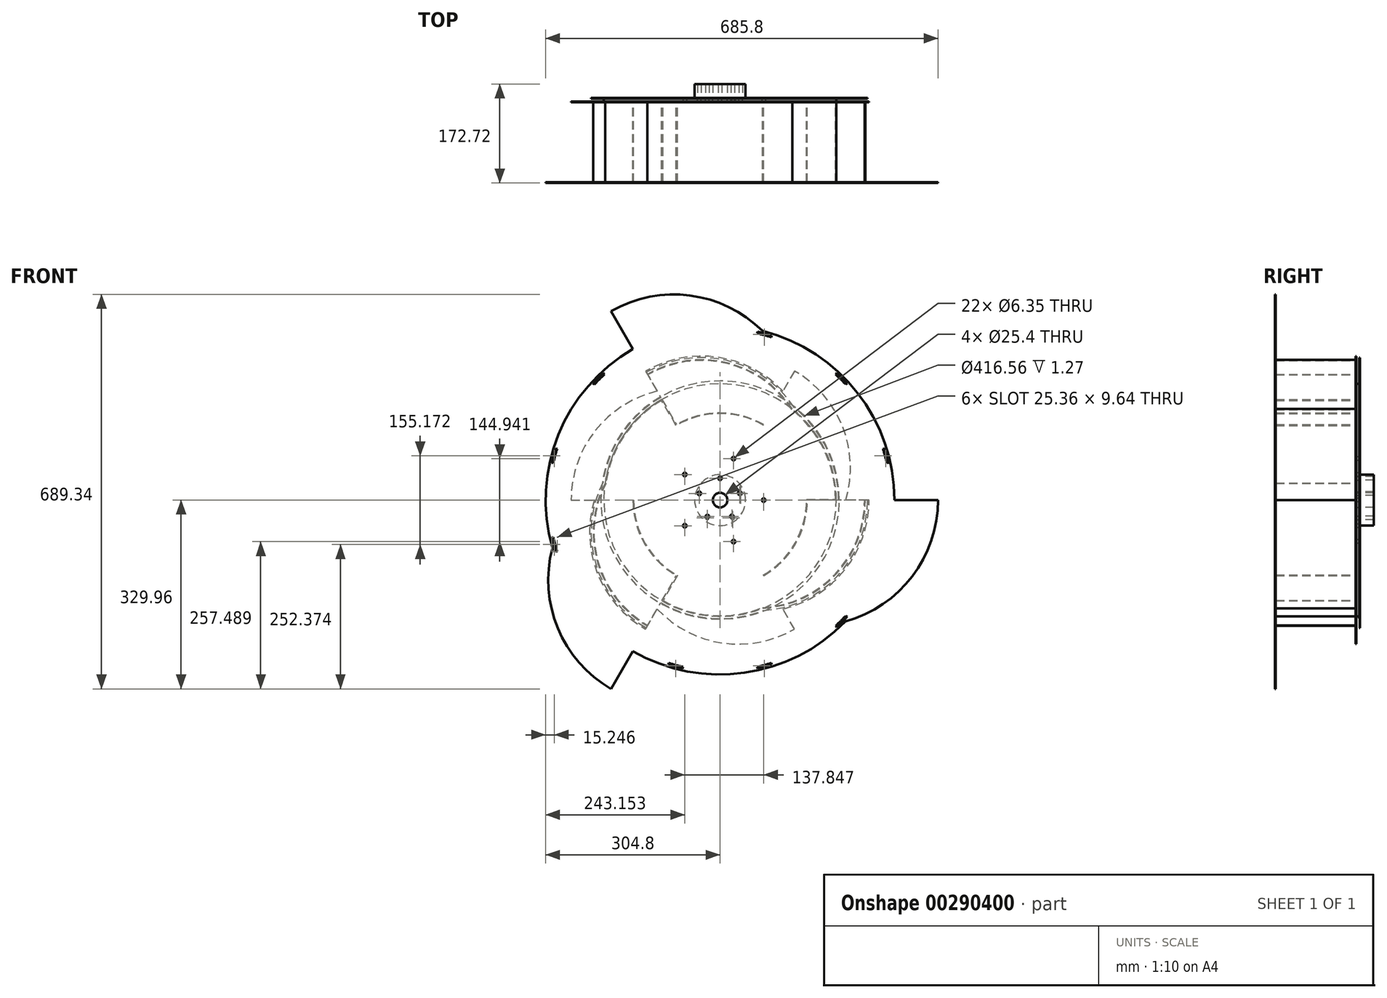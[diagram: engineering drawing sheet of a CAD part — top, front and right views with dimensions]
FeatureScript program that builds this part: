
annotation { "Feature Type Name" : "Feature", "Feature Type Description" : "" }
export const myFeature = defineFeature(function(context is Context, id is Id, definition is map)
    precondition{}
    {
        {
            var Q0;
            Q0=qCreatedBy(makeId("Front.planeOp"),FACE);
            var sketch = newSketch(context, id + "F0", { "sketchPlane" : qUnion([Q0])});
            skCircle(sketch, "E0", {"center": v(0, 0) * mm, "radius": 203.2 * mm});
            skCircle(sketch, "E1", {"center": v(0, 0) * mm, "radius": 12.7 * mm});
            skCircle(sketch, "E2", {"center": v(0, 38.1) * mm, "radius": 3.18 * mm});
            skCircle(sketch, "E3.1.0", {"center": v(-36.24, 11.77) * mm, "radius": 3.18 * mm});
            skCircle(sketch, "E3.2.0", {"center": v(-22.4, -30.82) * mm, "radius": 3.18 * mm});
            skCircle(sketch, "E3.3.0", {"center": v(22.4, -30.82) * mm, "radius": 3.18 * mm});
            skCircle(sketch, "E3.4.0", {"center": v(36.24, 11.77) * mm, "radius": 3.18 * mm});
            skLineSegment(sketch, "E4", {"start": v(0, 38.1) * mm, "end": v(36.24, 11.77) * mm, "construction": true});
            skLineSegment(sketch, "E5", {"start": v(36.24, 11.77) * mm, "end": v(22.4, -30.82) * mm, "construction": true});
            skLineSegment(sketch, "E6", {"start": v(22.4, -30.82) * mm, "end": v(-22.4, -30.82) * mm, "construction": true});
            skLineSegment(sketch, "E7", {"start": v(-22.4, -30.82) * mm, "end": v(-36.24, 11.77) * mm, "construction": true});
            skLineSegment(sketch, "E8", {"start": v(-36.24, 11.77) * mm, "end": v(0, 38.1) * mm, "construction": true});
            skSolve(sketch);
        }
        {
            var Q0;
            Q0=makeQuery(id+"F0.imprint","IMPRINT",FACE,{"disambiguationData":[TD([[makeQuery(id+"F0.imprint","IMPRINT",EDGE,{"derivedFrom":sQuery(id+"F0.wireOp",EDGE,"E0")}),1.0]])]});
            extrude(context, id + "F1", {"entities" : qUnion([Q0]), "depth" : 6.35 * mm});
        }
        {
            var Q0;
            Q0=makeQuery(id+"F1.opExtrude","CAP_FACE",FACE,{"disambiguationData":[OSD([sQuery(id+"F0.wireOp",EDGE,"E0"),sQuery(id+"F0.wireOp",EDGE,"E1"),sQuery(id+"F0.wireOp",EDGE,"E2"),sQuery(id+"F0.wireOp",EDGE,"E3.1.0"),sQuery(id+"F0.wireOp",EDGE,"E3.2.0"),sQuery(id+"F0.wireOp",EDGE,"E3.3.0"),sQuery(id+"F0.wireOp",EDGE,"E3.4.0")])],"isStart":true});
            var sketch = newSketch(context, id + "F2", { "sketchPlane" : qUnion([Q0])});
            skCircle(sketch, "E9", {"center": v(0, 0) * mm, "radius": 44.45 * mm});
            skCircle(sketch, "E10", {"center": v(0, 0) * mm, "radius": 12.7 * mm});
            skCircle(sketch, "E11", {"center": v(0, 38.1) * mm, "radius": 3.18 * mm});
            skCircle(sketch, "E12", {"center": v(36.24, 11.77) * mm, "radius": 3.18 * mm});
            skCircle(sketch, "E13", {"center": v(22.4, -30.82) * mm, "radius": 3.18 * mm});
            skCircle(sketch, "E14", {"center": v(-22.4, -30.82) * mm, "radius": 3.18 * mm});
            skCircle(sketch, "E15", {"center": v(-36.24, 11.77) * mm, "radius": 3.18 * mm});
            skSolve(sketch);
        }
        {
            var Q0;
            Q0=qSketchRegion(id+"F2",true);
            extrude(context, id + "F3", {"entities" : qUnion([Q0]), "depth" : 25.4 * mm});
        }
        {
            var Q0;
            Q0=makeQuery(id+"F3.opExtrude","CAP_FACE",FACE,{"disambiguationData":[OSD([sQuery(id+"F2.wireOp",EDGE,"E9"),sQuery(id+"F2.wireOp",EDGE,"E10"),sQuery(id+"F2.wireOp",EDGE,"E11"),sQuery(id+"F2.wireOp",EDGE,"E12"),sQuery(id+"F2.wireOp",EDGE,"E13"),sQuery(id+"F2.wireOp",EDGE,"E14"),sQuery(id+"F2.wireOp",EDGE,"E15")])],"isStart":false});
            cPlane(context, id + "F4", {"entities" : qUnion([Q0]), "cplaneType" : CPlaneType.OFFSET, "offset" : 25.4 * mm, "width" : 152.4 * mm, "height" : 152.4 * mm});
        }
        {
            var Q0;
            Q0=qCreatedBy(id+"F4.planeOp",FACE);
            var sketch = newSketch(context, id + "F5", { "sketchPlane" : qUnion([Q0])});
            skArc(sketch, "E16", {"start": v(-12.3, -3.17) * mm, "mid": v(12.7, 0) * mm, "end": v(-12.3, 3.17) * mm});
            skLineSegment(sketch, "E17", {"start": v(0, 0) * mm, "end": v(-12.7, 0) * mm, "construction": true});
            skLineSegment(sketch, "E18.bottom", {"start": v(-12.3, -3.18) * mm, "end": v(-9.76, -3.18) * mm});
            skLineSegment(sketch, "E18.top", {"start": v(-12.3, 3.17) * mm, "end": v(-9.76, 3.18) * mm});
            skLineSegment(sketch, "E18.right", {"start": v(-9.76, -3.17) * mm, "end": v(-9.76, 3.17) * mm});
            skLineSegment(sketch, "E19", {"start": v(-12.3, -3.17) * mm, "end": v(-12.3, 3.17) * mm, "construction": true});
            skSolve(sketch);
        }
        {
            var Q0;
            Q0=qSketchRegion(id+"F5",true);
            extrude(context, id + "F6", {"entities" : qUnion([Q0]), "oppositeDirection" : true, "depth" : 304.8 * mm});
        }
        {
            var Q0;
            Q0=makeQuery(id+"F1.opExtrude","CAP_FACE",FACE,{"disambiguationData":[OSD([sQuery(id+"F0.wireOp",EDGE,"E0"),sQuery(id+"F0.wireOp",EDGE,"E1"),sQuery(id+"F0.wireOp",EDGE,"E2"),sQuery(id+"F0.wireOp",EDGE,"E3.1.0"),sQuery(id+"F0.wireOp",EDGE,"E3.2.0"),sQuery(id+"F0.wireOp",EDGE,"E3.3.0"),sQuery(id+"F0.wireOp",EDGE,"E3.4.0")])],"isStart":false});
            var sketch = newSketch(context, id + "F7", { "sketchPlane" : qUnion([Q0])});
            skLineSegment(sketch, "E20", {"start": v(0, 0) * mm, "end": v(0, 203.2) * mm, "construction": true});
            skLineSegment(sketch, "E21", {"start": v(0, 203.2) * mm, "end": v(203.2, 0) * mm, "construction": true});
            skLineSegment(sketch, "E22", {"start": v(203.2, 0) * mm, "end": v(0, -203.2) * mm, "construction": true});
            skLineSegment(sketch, "E23", {"start": v(0, -203.2) * mm, "end": v(-203.2, 0) * mm, "construction": true});
            skLineSegment(sketch, "E24", {"start": v(-203.2, 0) * mm, "end": v(0, 203.2) * mm, "construction": true});
            skArc(sketch, "E25", {"start": v(0, 203.2) * mm, "mid": v(-143.68, 143.68) * mm, "end": v(-203.2, 0) * mm});
            skArc(sketch, "E26", {"start": v(0, 196.85) * mm, "mid": v(-139.2, 139.2) * mm, "end": v(-196.85, 0) * mm});
            skLineSegment(sketch, "E27", {"start": v(-203.2, 0) * mm, "end": v(-196.85, 0) * mm});
            skLineSegment(sketch, "E28", {"start": v(0, 203.2) * mm, "end": v(0, 196.85) * mm});
            skArc(sketch, "E29", {"start": v(279.4, 0) * mm, "mid": v(172.74, 147.03) * mm, "end": v(0, 203.2) * mm});
            skLineSegment(sketch, "E30", {"start": v(203.2, 0) * mm, "end": v(203.2, -92.56) * mm, "construction": true});
            skLineSegment(sketch, "E31", {"start": v(203.2, 0) * mm, "end": v(279.4, 0) * mm, "construction": true});
            skLineSegment(sketch, "E32", {"start": v(0, 203.2) * mm, "end": v(0, 209.55) * mm, "construction": true});
            skArc(sketch, "E33", {"start": v(0, 203.2) * mm, "mid": v(-38.81, 199.46) * mm, "end": v(-76.2, 188.37) * mm});
            skLineSegment(sketch, "E34", {"start": v(279.4, 0) * mm, "end": v(285.75, 0) * mm, "construction": true});
            skArc(sketch, "E35", {"start": v(285.75, 0) * mm, "mid": v(177.18, 151.55) * mm, "end": v(0, 209.55) * mm});
            skLineSegment(sketch, "E36", {"start": v(279.4, 0) * mm, "end": v(285.75, 0) * mm});
            skLineSegment(sketch, "E37", {"start": v(-76.2, 188.37) * mm, "end": v(-100.1, 178.7) * mm, "construction": true});
            skLineSegment(sketch, "E38", {"start": v(-76.2, 188.37) * mm, "end": v(-78.58, 194.26) * mm});
            skArc(sketch, "E39", {"start": v(0, 209.55) * mm, "mid": v(-40.03, 205.7) * mm, "end": v(-78.58, 194.26) * mm});
            skSolve(sketch);
        }
        {
            var Q0;
            Q0=qSketchRegion(id+"F7",true);
            extrude(context, id + "F8", {"entities" : qUnion([Q0]), "depth" : 152.4 * mm});
        }
        {
            var Q0;
            Q0=makeQuery(id+"F8.opExtrude","SWEPT_BODY",BODY,{"disambiguationData":[OSD([sQuery(id+"F7.wireOp",EDGE,"E25"),sQuery(id+"F7.wireOp",EDGE,"E26"),sQuery(id+"F7.wireOp",EDGE,"E27"),sQuery(id+"F7.wireOp",EDGE,"E28"),sQuery(id+"F7.wireOp",EDGE,"E29"),sQuery(id+"F7.wireOp",EDGE,"E35"),sQuery(id+"F7.wireOp",EDGE,"E36"),sQuery(id+"F7.wireOp",EDGE,"E38"),sQuery(id+"F7.wireOp",EDGE,"E39")])]});
            deleteBodies(context, id + "F9", {"entities" : qUnion([Q0])});
        }
        {
            var Q0;
            Q0=makeQuery(id+"F1.opExtrude","CAP_FACE",FACE,{"disambiguationData":[OSD([sQuery(id+"F0.wireOp",EDGE,"E0"),sQuery(id+"F0.wireOp",EDGE,"E1"),sQuery(id+"F0.wireOp",EDGE,"E2"),sQuery(id+"F0.wireOp",EDGE,"E3.1.0"),sQuery(id+"F0.wireOp",EDGE,"E3.2.0"),sQuery(id+"F0.wireOp",EDGE,"E3.3.0"),sQuery(id+"F0.wireOp",EDGE,"E3.4.0")])],"isStart":false});
            var sketch = newSketch(context, id + "F10", { "sketchPlane" : qUnion([Q0])});
            skLineSegment(sketch, "E40", {"start": v(0, 0) * mm, "end": v(203.2, 0) * mm, "construction": true});
            skLineSegment(sketch, "E41", {"start": v(203.2, 0) * mm, "end": v(203.2, 0) * mm});
            skLineSegment(sketch, "E42", {"start": v(203.2, 0) * mm, "end": v(524, 0) * mm, "construction": true});
            skArc(sketch, "E43", {"start": v(74.61, -189) * mm, "mid": v(202.01, -130.3) * mm, "end": v(254, 0) * mm});
            skLineSegment(sketch, "E44", {"start": v(0, 0) * mm, "end": v(-101.6, -175.98) * mm, "construction": true});
            skLineSegment(sketch, "E45", {"start": v(0, 0) * mm, "end": v(-101.6, 175.98) * mm, "construction": true});
            skLineSegment(sketch, "E46", {"start": v(-101.6, -175.98) * mm, "end": v(-76.2, -131.98) * mm});
            skArc(sketch, "E47", {"start": v(-152.4, 0) * mm, "mid": v(-131.98, -76.2) * mm, "end": v(-76.2, -131.98) * mm});
            skCircle(sketch, "E48", {"center": v(0, 0) * mm, "radius": 152.4 * mm, "construction": true});
            skLineSegment(sketch, "E49", {"start": v(-152.4, 0) * mm, "end": v(-151.13, 0) * mm});
            skArc(sketch, "E50", {"start": v(-151.13, 0) * mm, "mid": v(-130.56, -76.11) * mm, "end": v(-74.46, -131.51) * mm});
            skLineSegment(sketch, "E51", {"start": v(-74.46, -131.51) * mm, "end": v(-99.86, -175.5) * mm});
            skArc(sketch, "E52", {"start": v(74.34, -187.75) * mm, "mid": v(201.02, -129.5) * mm, "end": v(252.73, 0) * mm});
            skLineSegment(sketch, "E53", {"start": v(252.73, 0) * mm, "end": v(254, 0) * mm});
            skArc(sketch, "E54.trimOffspring", {"start": v(-101.6, 175.98) * mm, "mid": v(-182.99, -88.35) * mm, "end": v(74.61, -189) * mm, "construction": true});
            skArc(sketch, "E55", {"start": v(-99.86, -175.5) * mm, "mid": v(-14.15, -201.43) * mm, "end": v(74.34, -187.75) * mm});
            skArc(sketch, "E56", {"start": v(-101.6, -175.98) * mm, "mid": v(-14.98, -202.65) * mm, "end": v(74.61, -189) * mm});
            skArc(sketch, "E57.1.0", {"start": v(76.2, -131.98) * mm, "mid": v(131.98, -76.2) * mm, "end": v(152.4, 0) * mm});
            skArc(sketch, "E57.1.1", {"start": v(75.56, -130.88) * mm, "mid": v(131.2, -75.01) * mm, "end": v(151.12, 1.27) * mm});
            skLineSegment(sketch, "E57.1.2", {"start": v(151.12, 1.27) * mm, "end": v(201.93, 1.27) * mm});
            skArc(sketch, "E57.1.3", {"start": v(201.93, 1.27) * mm, "mid": v(181.52, 88.46) * mm, "end": v(125.43, 158.25) * mm});
            skLineSegment(sketch, "E57.1.4", {"start": v(203.2, 0) * mm, "end": v(152.4, 0) * mm});
            skArc(sketch, "E57.1.5", {"start": v(203.2, 0) * mm, "mid": v(182.99, 88.35) * mm, "end": v(126.38, 159.12) * mm});
            skArc(sketch, "E57.1.6", {"start": v(126.38, 159.12) * mm, "mid": v(11.83, 240.1) * mm, "end": v(-127, 219.97) * mm});
            skArc(sketch, "E57.1.7", {"start": v(125.43, 158.25) * mm, "mid": v(11.63, 238.84) * mm, "end": v(-126.36, 218.87) * mm});
            skLineSegment(sketch, "E57.1.8", {"start": v(-126.36, 218.87) * mm, "end": v(-127, 219.97) * mm});
            skArc(sketch, "E57.2.0", {"start": v(76.2, 131.98) * mm, "mid": v(0, 152.4) * mm, "end": v(-76.2, 131.98) * mm});
            skArc(sketch, "E57.2.1", {"start": v(75.57, 130.88) * mm, "mid": v(-0.64, 151.13) * mm, "end": v(-76.66, 130.24) * mm});
            skLineSegment(sketch, "E57.2.2", {"start": v(-76.66, 130.24) * mm, "end": v(-102.06, 174.24) * mm});
            skArc(sketch, "E57.2.3", {"start": v(-102.06, 174.24) * mm, "mid": v(-167.37, 112.97) * mm, "end": v(-199.76, 29.5) * mm});
            skLineSegment(sketch, "E57.2.4", {"start": v(-101.6, 175.98) * mm, "end": v(-76.2, 131.98) * mm});
            skArc(sketch, "E57.2.5", {"start": v(-101.6, 175.98) * mm, "mid": v(-168, 114.3) * mm, "end": v(-201, 29.89) * mm});
            skArc(sketch, "E57.2.6", {"start": v(-201, 29.89) * mm, "mid": v(-213.84, -109.8) * mm, "end": v(-127, -219.97) * mm});
            skArc(sketch, "E57.2.7", {"start": v(-199.76, 29.5) * mm, "mid": v(-212.65, -109.34) * mm, "end": v(-126.37, -218.87) * mm});
            skLineSegment(sketch, "E57.2.8", {"start": v(-126.37, -218.87) * mm, "end": v(-127, -219.97) * mm});
            skLineSegment(sketch, "E58", {"start": v(75.56, -130.88) * mm, "end": v(76.2, -131.98) * mm});
            skLineSegment(sketch, "E59", {"start": v(75.57, 130.88) * mm, "end": v(76.2, 131.98) * mm});
            skSolve(sketch);
        }
        {
            var Q0;
            Q0=qSketchRegion(id+"F10",true);
            extrude(context, id + "F11", {"entities" : qUnion([Q0]), "depth" : 139.7 * mm});
        }
        {
            var Q0;
            Q0=makeQuery(id+"F11.opExtrude","CAP_FACE",FACE,{"disambiguationData":[OSD([sQuery(id+"F10.wireOp",EDGE,"E57.2.0"),sQuery(id+"F10.wireOp",EDGE,"E57.2.1"),sQuery(id+"F10.wireOp",EDGE,"E57.2.2"),sQuery(id+"F10.wireOp",EDGE,"E57.2.3"),sQuery(id+"F10.wireOp",EDGE,"E57.2.4"),sQuery(id+"F10.wireOp",EDGE,"E57.2.5"),sQuery(id+"F10.wireOp",EDGE,"E57.2.6"),sQuery(id+"F10.wireOp",EDGE,"E57.2.7"),sQuery(id+"F10.wireOp",EDGE,"E57.2.8"),sQuery(id+"F10.wireOp",EDGE,"E59")])],"isStart":false});
            var sketch = newSketch(context, id + "F12", { "sketchPlane" : qUnion([Q0])});
            skArc(sketch, "E60", {"start": v(-152.4, -263.96) * mm, "mid": v(42.3, -301.85) * mm, "end": v(219.07, -211.92) * mm});
            skArc(sketch, "E61", {"start": v(-293.06, -83.77) * mm, "mid": v(-283.43, -224.21) * mm, "end": v(-190.5, -329.96) * mm});
            skLineSegment(sketch, "E62", {"start": v(-190.5, -329.96) * mm, "end": v(-152.4, -263.96) * mm});
            skLineSegment(sketch, "E63", {"start": v(-152.4, -263.96) * mm, "end": v(-59.03, -317.87) * mm, "construction": true});
            skArc(sketch, "E64.1.0", {"start": v(219.07, -211.92) * mm, "mid": v(335.89, -133.35) * mm, "end": v(381, 0) * mm});
            skLineSegment(sketch, "E64.1.1", {"start": v(381, 0) * mm, "end": v(304.8, 0) * mm});
            skArc(sketch, "E64.2.0", {"start": v(73.99, 295.68) * mm, "mid": v(-52.46, 357.56) * mm, "end": v(-190.5, 329.96) * mm});
            skLineSegment(sketch, "E64.2.1", {"start": v(-190.5, 329.96) * mm, "end": v(-152.4, 263.96) * mm});
            skArc(sketch, "E65.trimOffspring", {"start": v(304.8, 0) * mm, "mid": v(240.27, 187.55) * mm, "end": v(73.99, 295.68) * mm});
            skArc(sketch, "E66.trimOffspring", {"start": v(-152.4, 263.96) * mm, "mid": v(-282.56, 114.3) * mm, "end": v(-293.06, -83.77) * mm});
            skSolve(sketch);
        }
        {
            var Q0;
            Q0=qSketchRegion(id+"F12",true);
            extrude(context, id + "F13", {"entities" : qUnion([Q0]), "depth" : 1.27 * mm});
        }
        {
            var Q0;
            Q0=makeQuery(id+"F13.opExtrude","CAP_FACE",FACE,{"disambiguationData":[OSD([sQuery(id+"F12.wireOp",EDGE,"E60"),sQuery(id+"F12.wireOp",EDGE,"E61"),sQuery(id+"F12.wireOp",EDGE,"E62"),sQuery(id+"F12.wireOp",EDGE,"E64.1.0"),sQuery(id+"F12.wireOp",EDGE,"E64.1.1"),sQuery(id+"F12.wireOp",EDGE,"E64.2.0"),sQuery(id+"F12.wireOp",EDGE,"E64.2.1"),sQuery(id+"F12.wireOp",EDGE,"E65.trimOffspring"),sQuery(id+"F12.wireOp",EDGE,"E66.trimOffspring")])],"isStart":false});
            var sketch = newSketch(context, id + "F14", { "sketchPlane" : qUnion([Q0])});
            skCircle(sketch, "E67", {"center": v(0, 0) * mm, "radius": 76.2 * mm, "construction": true});
            skCircle(sketch, "E68", {"center": v(76.2, 0) * mm, "radius": 3.18 * mm});
            skCircle(sketch, "E69.1.0", {"center": v(23.55, 72.47) * mm, "radius": 3.18 * mm});
            skCircle(sketch, "E69.2.0", {"center": v(-61.65, 44.79) * mm, "radius": 3.18 * mm});
            skCircle(sketch, "E69.3.0", {"center": v(-61.65, -44.79) * mm, "radius": 3.18 * mm});
            skCircle(sketch, "E69.4.0", {"center": v(23.55, -72.47) * mm, "radius": 3.18 * mm});
            skLineSegment(sketch, "E70", {"start": v(0, 0) * mm, "end": v(0, 176.8) * mm, "construction": true});
            skCircle(sketch, "E71", {"center": v(0, 0) * mm, "radius": 12.7 * mm});
            skSolve(sketch);
        }
        {
            var Q0;
            Q0=qSketchRegion(id+"F14",true);
            extrude(context, id + "F15", {"entities" : qUnion([Q0]), "operationType" : NewBodyOperationType.REMOVE, "endBound" : BoundingType.THROUGH_ALL, "oppositeDirection" : true, "depth" : 25.4 * mm});
        }
        {
            var Q0;
            Q0=makeQuery(id+"F13.opExtrude","CAP_FACE",FACE,{"disambiguationData":[OSD([sQuery(id+"F12.wireOp",EDGE,"E60"),sQuery(id+"F12.wireOp",EDGE,"E61"),sQuery(id+"F12.wireOp",EDGE,"E62"),sQuery(id+"F12.wireOp",EDGE,"E64.1.0"),sQuery(id+"F12.wireOp",EDGE,"E64.1.1"),sQuery(id+"F12.wireOp",EDGE,"E64.2.0"),sQuery(id+"F12.wireOp",EDGE,"E64.2.1"),sQuery(id+"F12.wireOp",EDGE,"E65.trimOffspring"),sQuery(id+"F12.wireOp",EDGE,"E66.trimOffspring")])],"isStart":true});
            var sketch = newSketch(context, id + "F16", { "sketchPlane" : qUnion([Q0])});
            skCircle(sketch, "E72", {"center": v(-23.55, -72.47) * mm, "radius": 6.35 * mm});
            skCircle(sketch, "E73", {"center": v(0, 0) * mm, "radius": 76.2 * mm, "construction": true});
            skCircle(sketch, "E74.1.0", {"center": v(61.65, -44.79) * mm, "radius": 6.35 * mm});
            skCircle(sketch, "E74.2.0", {"center": v(61.65, 44.79) * mm, "radius": 6.35 * mm});
            skCircle(sketch, "E74.3.0", {"center": v(-23.55, 72.47) * mm, "radius": 6.35 * mm});
            skCircle(sketch, "E74.4.0", {"center": v(-76.2, 0) * mm, "radius": 6.35 * mm});
            skSolve(sketch);
        }
        {
            var Q0;
            Q0=makeQuery(id+"F13.opExtrude","CAP_FACE",FACE,{"disambiguationData":[OSD([sQuery(id+"F12.wireOp",EDGE,"E60"),sQuery(id+"F12.wireOp",EDGE,"E61"),sQuery(id+"F12.wireOp",EDGE,"E62"),sQuery(id+"F12.wireOp",EDGE,"E64.1.0"),sQuery(id+"F12.wireOp",EDGE,"E64.1.1"),sQuery(id+"F12.wireOp",EDGE,"E64.2.0"),sQuery(id+"F12.wireOp",EDGE,"E64.2.1"),sQuery(id+"F12.wireOp",EDGE,"E65.trimOffspring"),sQuery(id+"F12.wireOp",EDGE,"E66.trimOffspring")])],"isStart":false});
            var sketch = newSketch(context, id + "F17", { "sketchPlane" : qUnion([Q0])});
            skCircle(sketch, "E75", {"center": v(0, 0) * mm, "radius": 304.8 * mm, "construction": true});
            skLineSegment(sketch, "E76", {"start": v(0, 0) * mm, "end": v(0, 304.8) * mm, "construction": true});
            skLineSegment(sketch, "E77", {"start": v(73.99, 295.68) * mm, "end": v(213.6, 260.75) * mm, "construction": true});
            skLineSegment(sketch, "E78", {"start": v(0, 0) * mm, "end": v(215.53, 215.53) * mm, "construction": true});
            skArc(sketch, "E79", {"start": v(222.07, 204.11) * mm, "mid": v(213.28, 213.28) * mm, "end": v(204.11, 222.07) * mm});
            skPoint(sketch, "E80", {"position": v(213.28, 213.28) * mm});
            skArc(sketch, "E81", {"start": v(219.83, 201.86) * mm, "mid": v(211.04, 211.04) * mm, "end": v(201.86, 219.83) * mm});
            skPoint(sketch, "E82", {"position": v(211.04, 211.04) * mm});
            skLineSegment(sketch, "E83", {"start": v(204.11, 222.07) * mm, "end": v(201.86, 219.83) * mm});
            skLineSegment(sketch, "E84", {"start": v(222.07, 204.11) * mm, "end": v(219.83, 201.86) * mm});
            skLineSegment(sketch, "E85", {"start": v(211.04, 211.04) * mm, "end": v(233.3, 188.78) * mm, "construction": true});
            skArc(sketch, "E86.1.0", {"start": v(294.38, 65.73) * mm, "mid": v(291.35, 78.07) * mm, "end": v(287.8, 90.26) * mm});
            skPoint(sketch, "E86.1.1", {"position": v(288.28, 77.24) * mm});
            skPoint(sketch, "E86.1.2", {"position": v(291.35, 78.07) * mm});
            skArc(sketch, "E86.1.3", {"start": v(291.3, 64.9) * mm, "mid": v(288.28, 77.24) * mm, "end": v(284.73, 89.44) * mm});
            skLineSegment(sketch, "E86.1.4", {"start": v(294.38, 65.73) * mm, "end": v(291.3, 64.9) * mm});
            skLineSegment(sketch, "E86.1.5", {"start": v(287.8, 90.26) * mm, "end": v(284.73, 89.44) * mm});
            skArc(sketch, "E86.2.0", {"start": v(287.8, -90.26) * mm, "mid": v(291.35, -78.07) * mm, "end": v(294.38, -65.73) * mm, "construction": true});
            skPoint(sketch, "E86.2.1", {"position": v(288.28, -77.24) * mm});
            skPoint(sketch, "E86.2.2", {"position": v(291.35, -78.07) * mm});
            skArc(sketch, "E86.2.3", {"start": v(284.73, -89.44) * mm, "mid": v(288.28, -77.24) * mm, "end": v(291.3, -64.9) * mm, "construction": true});
            skLineSegment(sketch, "E86.2.4", {"start": v(287.8, -90.26) * mm, "end": v(284.73, -89.44) * mm, "construction": true});
            skLineSegment(sketch, "E86.2.5", {"start": v(294.38, -65.73) * mm, "end": v(291.3, -64.9) * mm, "construction": true});
            skArc(sketch, "E86.3.0", {"start": v(204.11, -222.07) * mm, "mid": v(213.28, -213.28) * mm, "end": v(222.07, -204.11) * mm});
            skPoint(sketch, "E86.3.1", {"position": v(211.04, -211.04) * mm});
            skPoint(sketch, "E86.3.2", {"position": v(213.28, -213.28) * mm});
            skArc(sketch, "E86.3.3", {"start": v(201.86, -219.83) * mm, "mid": v(211.04, -211.04) * mm, "end": v(219.83, -201.86) * mm});
            skLineSegment(sketch, "E86.3.4", {"start": v(204.11, -222.07) * mm, "end": v(201.86, -219.83) * mm});
            skLineSegment(sketch, "E86.3.5", {"start": v(222.07, -204.11) * mm, "end": v(219.83, -201.86) * mm});
            skArc(sketch, "E86.4.0", {"start": v(65.73, -294.38) * mm, "mid": v(78.07, -291.35) * mm, "end": v(90.26, -287.8) * mm});
            skPoint(sketch, "E86.4.1", {"position": v(77.24, -288.28) * mm});
            skPoint(sketch, "E86.4.2", {"position": v(78.07, -291.35) * mm});
            skArc(sketch, "E86.4.3", {"start": v(64.9, -291.3) * mm, "mid": v(77.24, -288.28) * mm, "end": v(89.44, -284.73) * mm});
            skLineSegment(sketch, "E86.4.4", {"start": v(65.73, -294.38) * mm, "end": v(64.9, -291.3) * mm});
            skLineSegment(sketch, "E86.4.5", {"start": v(90.26, -287.8) * mm, "end": v(89.44, -284.73) * mm});
            skArc(sketch, "E86.5.0", {"start": v(-90.26, -287.8) * mm, "mid": v(-78.07, -291.35) * mm, "end": v(-65.73, -294.38) * mm});
            skPoint(sketch, "E86.5.1", {"position": v(-77.24, -288.28) * mm});
            skPoint(sketch, "E86.5.2", {"position": v(-78.07, -291.35) * mm});
            skArc(sketch, "E86.5.3", {"start": v(-89.44, -284.73) * mm, "mid": v(-77.24, -288.28) * mm, "end": v(-64.9, -291.3) * mm});
            skLineSegment(sketch, "E86.5.4", {"start": v(-90.26, -287.8) * mm, "end": v(-89.44, -284.73) * mm});
            skLineSegment(sketch, "E86.5.5", {"start": v(-65.73, -294.38) * mm, "end": v(-64.9, -291.3) * mm});
            skArc(sketch, "E86.6.0", {"start": v(-222.07, -204.11) * mm, "mid": v(-213.28, -213.28) * mm, "end": v(-204.11, -222.07) * mm, "construction": true});
            skPoint(sketch, "E86.6.1", {"position": v(-211.04, -211.04) * mm});
            skPoint(sketch, "E86.6.2", {"position": v(-213.28, -213.28) * mm});
            skArc(sketch, "E86.6.3", {"start": v(-219.83, -201.86) * mm, "mid": v(-211.04, -211.04) * mm, "end": v(-201.86, -219.83) * mm, "construction": true});
            skLineSegment(sketch, "E86.6.4", {"start": v(-222.07, -204.11) * mm, "end": v(-219.83, -201.86) * mm, "construction": true});
            skLineSegment(sketch, "E86.6.5", {"start": v(-204.11, -222.07) * mm, "end": v(-201.86, -219.83) * mm, "construction": true});
            skArc(sketch, "E86.7.0", {"start": v(-294.38, -65.73) * mm, "mid": v(-291.35, -78.07) * mm, "end": v(-287.8, -90.26) * mm});
            skPoint(sketch, "E86.7.1", {"position": v(-288.28, -77.24) * mm});
            skPoint(sketch, "E86.7.2", {"position": v(-291.35, -78.07) * mm});
            skArc(sketch, "E86.7.3", {"start": v(-291.3, -64.9) * mm, "mid": v(-288.28, -77.24) * mm, "end": v(-284.73, -89.44) * mm});
            skLineSegment(sketch, "E86.7.4", {"start": v(-294.38, -65.73) * mm, "end": v(-291.3, -64.9) * mm});
            skLineSegment(sketch, "E86.7.5", {"start": v(-287.8, -90.26) * mm, "end": v(-284.73, -89.44) * mm});
            skArc(sketch, "E86.8.0", {"start": v(-287.8, 90.26) * mm, "mid": v(-291.35, 78.07) * mm, "end": v(-294.38, 65.73) * mm});
            skPoint(sketch, "E86.8.1", {"position": v(-288.28, 77.24) * mm});
            skPoint(sketch, "E86.8.2", {"position": v(-291.35, 78.07) * mm});
            skArc(sketch, "E86.8.3", {"start": v(-284.73, 89.44) * mm, "mid": v(-288.28, 77.24) * mm, "end": v(-291.3, 64.9) * mm});
            skLineSegment(sketch, "E86.8.4", {"start": v(-287.8, 90.26) * mm, "end": v(-284.73, 89.44) * mm});
            skLineSegment(sketch, "E86.8.5", {"start": v(-294.38, 65.73) * mm, "end": v(-291.3, 64.9) * mm});
            skArc(sketch, "E86.9.0", {"start": v(-204.11, 222.07) * mm, "mid": v(-213.28, 213.28) * mm, "end": v(-222.07, 204.11) * mm});
            skPoint(sketch, "E86.9.1", {"position": v(-211.04, 211.04) * mm});
            skPoint(sketch, "E86.9.2", {"position": v(-213.28, 213.28) * mm});
            skArc(sketch, "E86.9.3", {"start": v(-201.86, 219.83) * mm, "mid": v(-211.04, 211.04) * mm, "end": v(-219.83, 201.86) * mm});
            skLineSegment(sketch, "E86.9.4", {"start": v(-204.11, 222.07) * mm, "end": v(-201.86, 219.83) * mm});
            skLineSegment(sketch, "E86.9.5", {"start": v(-222.07, 204.11) * mm, "end": v(-219.83, 201.86) * mm});
            skArc(sketch, "E86.10.0", {"start": v(-65.73, 294.38) * mm, "mid": v(-78.07, 291.35) * mm, "end": v(-90.26, 287.8) * mm});
            skPoint(sketch, "E86.10.1", {"position": v(-77.24, 288.28) * mm});
            skPoint(sketch, "E86.10.2", {"position": v(-78.07, 291.35) * mm});
            skArc(sketch, "E86.10.3", {"start": v(-64.9, 291.3) * mm, "mid": v(-77.24, 288.28) * mm, "end": v(-89.44, 284.73) * mm});
            skLineSegment(sketch, "E86.10.4", {"start": v(-65.73, 294.38) * mm, "end": v(-64.9, 291.3) * mm, "construction": true});
            skLineSegment(sketch, "E86.10.5", {"start": v(-90.26, 287.8) * mm, "end": v(-89.44, 284.73) * mm, "construction": true});
            skArc(sketch, "E86.11.0", {"start": v(90.26, 287.8) * mm, "mid": v(78.07, 291.35) * mm, "end": v(65.73, 294.38) * mm});
            skPoint(sketch, "E86.11.1", {"position": v(77.24, 288.28) * mm});
            skPoint(sketch, "E86.11.2", {"position": v(78.07, 291.35) * mm});
            skArc(sketch, "E86.11.3", {"start": v(89.44, 284.73) * mm, "mid": v(77.24, 288.28) * mm, "end": v(64.9, 291.3) * mm});
            skLineSegment(sketch, "E86.11.4", {"start": v(90.26, 287.8) * mm, "end": v(89.44, 284.73) * mm});
            skLineSegment(sketch, "E86.11.5", {"start": v(65.73, 294.38) * mm, "end": v(64.9, 291.3) * mm});
            skLineSegment(sketch, "E86.anchor1", {"start": v(0, 0) * mm, "end": v(219.83, 201.86) * mm, "construction": true});
            skLineSegment(sketch, "E86.anchor2", {"start": v(0, 0) * mm, "end": v(89.44, 284.73) * mm, "construction": true});
            skLineSegment(sketch, "E87", {"start": v(0, 0) * mm, "end": v(-78.89, 294.41) * mm});
            skSolve(sketch);
        }
        {
            var Q0;
            Q0=qSketchRegion(id+"F17",true);
            extrude(context, id + "F18", {"entities" : qUnion([Q0]), "operationType" : NewBodyOperationType.REMOVE, "oppositeDirection" : true, "depth" : 25.4 * mm});
        }
        {
            var Q0;
            Q0=makeQuery(id+"F11.opExtrude","CAP_FACE",FACE,{"disambiguationData":[OSD([sQuery(id+"F10.wireOp",EDGE,"E57.2.0"),sQuery(id+"F10.wireOp",EDGE,"E57.2.1"),sQuery(id+"F10.wireOp",EDGE,"E57.2.2"),sQuery(id+"F10.wireOp",EDGE,"E57.2.3"),sQuery(id+"F10.wireOp",EDGE,"E57.2.4"),sQuery(id+"F10.wireOp",EDGE,"E57.2.5"),sQuery(id+"F10.wireOp",EDGE,"E57.2.6"),sQuery(id+"F10.wireOp",EDGE,"E57.2.7"),sQuery(id+"F10.wireOp",EDGE,"E57.2.8"),sQuery(id+"F10.wireOp",EDGE,"E59")])],"isStart":true});
            var sketch = newSketch(context, id + "F19", { "sketchPlane" : qUnion([Q0])});
            skCircle(sketch, "E88", {"center": v(0, 0) * mm, "radius": 208.28 * mm});
            skArc(sketch, "E89", {"start": v(-260.35, 0) * mm, "mid": v(-205.56, -135.77) * mm, "end": v(-71.88, -195.48) * mm});
            skLineSegment(sketch, "E90", {"start": v(-254, 0) * mm, "end": v(-413.2, 0) * mm, "construction": true});
            skLineSegment(sketch, "E91", {"start": v(-260.35, 0) * mm, "end": v(-208.28, 0) * mm});
            skLineSegment(sketch, "E92.1.0", {"start": v(-130.18, -225.47) * mm, "end": v(-104.14, -180.38) * mm});
            skArc(sketch, "E92.1.1", {"start": v(-130.17, -225.47) * mm, "mid": v(14.8, -245.9) * mm, "end": v(133.35, -160) * mm});
            skLineSegment(sketch, "E92.2.0", {"start": v(130.17, -225.47) * mm, "end": v(104.14, -180.38) * mm});
            skArc(sketch, "E92.2.1", {"start": v(130.18, -225.47) * mm, "mid": v(220.36, -110.13) * mm, "end": v(205.23, 35.5) * mm});
            skLineSegment(sketch, "E92.3.0", {"start": v(260.35, 0) * mm, "end": v(208.28, 0) * mm});
            skArc(sketch, "E92.3.1", {"start": v(260.35, 0) * mm, "mid": v(205.56, 135.77) * mm, "end": v(71.88, 195.48) * mm});
            skLineSegment(sketch, "E92.4.0", {"start": v(130.17, 225.47) * mm, "end": v(104.14, 180.38) * mm});
            skArc(sketch, "E92.4.1", {"start": v(130.17, 225.47) * mm, "mid": v(-14.8, 245.9) * mm, "end": v(-133.35, 160) * mm});
            skLineSegment(sketch, "E92.5.0", {"start": v(-130.17, 225.47) * mm, "end": v(-104.14, 180.38) * mm});
            skArc(sketch, "E92.5.1", {"start": v(-130.18, 225.47) * mm, "mid": v(-220.36, 110.13) * mm, "end": v(-205.23, -35.5) * mm});
            skSolve(sketch);
        }
        {
            var Q0;
            Q0 = qSketchRegion(id + "F19", true);
            extrude(context, id + "F20", {"entities" : qUnion([Q0]), "depth" : 1.27 * mm});
        }
        {
            var Q0;
            Q0=makeQuery(id+"F20.opExtrude","CAP_FACE",FACE,{"disambiguationData":[OSD([sQuery(id+"F19.wireOp",EDGE,"E88"),sQuery(id+"F19.wireOp",EDGE,"E89"),sQuery(id+"F19.wireOp",EDGE,"E91"),sQuery(id+"F19.wireOp",EDGE,"E92.1.0"),sQuery(id+"F19.wireOp",EDGE,"E92.1.1"),sQuery(id+"F19.wireOp",EDGE,"E92.2.0"),sQuery(id+"F19.wireOp",EDGE,"E92.2.1"),sQuery(id+"F19.wireOp",EDGE,"E92.3.0"),sQuery(id+"F19.wireOp",EDGE,"E92.3.1"),sQuery(id+"F19.wireOp",EDGE,"E92.4.0"),sQuery(id+"F19.wireOp",EDGE,"E92.4.1"),sQuery(id+"F19.wireOp",EDGE,"E92.5.0"),sQuery(id+"F19.wireOp",EDGE,"E92.5.1")])],"isStart":false});
            var sketch = newSketch(context, id + "F21", { "sketchPlane" : qUnion([Q0])});
            skCircle(sketch, "E93", {"center": v(0, 0) * mm, "radius": 12.7 * mm});
            skCircle(sketch, "E94", {"center": v(36.24, 11.77) * mm, "radius": 3.18 * mm});
            skCircle(sketch, "E95.1.0", {"center": v(22.2, -28.72) * mm, "radius": 3.18 * mm});
            skCircle(sketch, "E95.2.0", {"center": v(-20.66, -28.44) * mm, "radius": 3.18 * mm});
            skCircle(sketch, "E95.3.0", {"center": v(-34.17, 12.23) * mm, "radius": 3.18 * mm});
            skCircle(sketch, "E95.4.0", {"center": v(0, 38.1) * mm, "radius": 3.18 * mm});
            skPoint(sketch, "E95.center", {"position": v(0.96, 1.33) * mm});
            skLineSegment(sketch, "E95.anchor1", {"start": v(0.96, 1.33) * mm, "end": v(36.24, 11.77) * mm, "construction": true});
            skLineSegment(sketch, "E95.anchor2", {"start": v(0.96, 1.33) * mm, "end": v(0, 38.1) * mm, "construction": true});
            skSolve(sketch);
        }
        {
            var Q0;
            Q0 = qSketchRegion(id + "F21", true);
            extrude(context, id + "F22", {"entities" : qUnion([Q0]), "operationType" : NewBodyOperationType.REMOVE, "endBound" : BoundingType.THROUGH_ALL, "oppositeDirection" : true, "depth" : 25.4 * mm});
        }
        {
            var Q0;
            Q0=makeQuery(id+"F1.opExtrude","CAP_FACE",FACE,{"disambiguationData":[OSD([sQuery(id+"F0.wireOp",EDGE,"E0"),sQuery(id+"F0.wireOp",EDGE,"E1"),sQuery(id+"F0.wireOp",EDGE,"E2"),sQuery(id+"F0.wireOp",EDGE,"E3.1.0"),sQuery(id+"F0.wireOp",EDGE,"E3.2.0"),sQuery(id+"F0.wireOp",EDGE,"E3.3.0"),sQuery(id+"F0.wireOp",EDGE,"E3.4.0")])],"isStart":true});
            var sketch = newSketch(context, id + "F23", { "sketchPlane" : qUnion([Q0])});
            skArc(sketch, "E96", {"start": v(128.9, 223.27) * mm, "mid": v(-18.27, 242.38) * mm, "end": v(-135.52, 151.4) * mm});
            skLineSegment(sketch, "E97", {"start": v(126.36, 218.87) * mm, "end": v(128.9, 223.27) * mm, "construction": true});
            skLineSegment(sketch, "E98", {"start": v(128.9, 223.27) * mm, "end": v(101.6, 175.98) * mm});
            skArc(sketch, "E99", {"start": v(204.67, 31.06) * mm, "mid": v(170.98, 116.7) * mm, "end": v(103.5, 179.28) * mm});
            skArc(sketch, "E100.1.0", {"start": v(-257.81, 0) * mm, "mid": v(-200.77, -137) * mm, "end": v(-63.36, -193.07) * mm});
            skArc(sketch, "E100.2.0", {"start": v(128.9, -223.27) * mm, "mid": v(219.04, -105.37) * mm, "end": v(198.88, 41.66) * mm});
            skLineSegment(sketch, "E101.1.0", {"start": v(-257.81, 0) * mm, "end": v(-203.2, 0) * mm});
            skArc(sketch, "E101.1.1", {"start": v(-129.23, 161.72) * mm, "mid": v(-186.56, 89.72) * mm, "end": v(-207.01, 0) * mm});
            skLineSegment(sketch, "E101.2.0", {"start": v(128.9, -223.27) * mm, "end": v(101.6, -175.98) * mm});
            skArc(sketch, "E101.2.1", {"start": v(-75.43, -192.78) * mm, "mid": v(15.58, -206.42) * mm, "end": v(103.5, -179.28) * mm});
            skCircle(sketch, "E102", {"center": v(0, 0) * mm, "radius": 12.7 * mm});
            skSolve(sketch);
        }
        {
            var Q0;
            Q0 = qSketchRegion(id + "F23", true);
            extrude(context, id + "F24", {"entities" : qUnion([Q0]), "depth" : 1.27 * mm});
        }
        {
            var Q0;
            Q0=makeQuery(id+"F20.opExtrude","CAP_FACE",FACE,{"disambiguationData":[OSD([sQuery(id+"F19.wireOp",EDGE,"E88"),sQuery(id+"F19.wireOp",EDGE,"E89"),sQuery(id+"F19.wireOp",EDGE,"E91"),sQuery(id+"F19.wireOp",EDGE,"E92.1.0"),sQuery(id+"F19.wireOp",EDGE,"E92.1.1"),sQuery(id+"F19.wireOp",EDGE,"E92.2.0"),sQuery(id+"F19.wireOp",EDGE,"E92.2.1"),sQuery(id+"F19.wireOp",EDGE,"E92.3.0"),sQuery(id+"F19.wireOp",EDGE,"E92.3.1"),sQuery(id+"F19.wireOp",EDGE,"E92.4.0"),sQuery(id+"F19.wireOp",EDGE,"E92.4.1"),sQuery(id+"F19.wireOp",EDGE,"E92.5.0"),sQuery(id+"F19.wireOp",EDGE,"E92.5.1")])],"isStart":false});
            var sketch = newSketch(context, id + "F25", { "sketchPlane" : qUnion([Q0])});
            skCircle(sketch, "E103", {"center": v(0, 0) * mm, "radius": 208.28 * mm});
            skSolve(sketch);
        }
        {
            var Q0;
            Q0 = qSketchRegion(id + "F25", true);
            var Q1;
            Q1=makeQuery(id+"F20.opExtrude","CAP_FACE",FACE,{"disambiguationData":[OSD([sQuery(id+"F19.wireOp",EDGE,"E88"),sQuery(id+"F19.wireOp",EDGE,"E89"),sQuery(id+"F19.wireOp",EDGE,"E91"),sQuery(id+"F19.wireOp",EDGE,"E92.1.0"),sQuery(id+"F19.wireOp",EDGE,"E92.1.1"),sQuery(id+"F19.wireOp",EDGE,"E92.2.0"),sQuery(id+"F19.wireOp",EDGE,"E92.2.1"),sQuery(id+"F19.wireOp",EDGE,"E92.3.0"),sQuery(id+"F19.wireOp",EDGE,"E92.3.1"),sQuery(id+"F19.wireOp",EDGE,"E92.4.0"),sQuery(id+"F19.wireOp",EDGE,"E92.4.1"),sQuery(id+"F19.wireOp",EDGE,"E92.5.0"),sQuery(id+"F19.wireOp",EDGE,"E92.5.1")])],"isStart":true});
            extrude(context, id + "F26", {"entities" : qUnion([Q0]), "endBound" : BoundingType.UP_TO_SURFACE, "oppositeDirection" : true, "depth" : 25.4 * mm, "endBoundEntityFace" : qUnion([Q1]), "offsetDistance" : 25.4 * mm});
        }
    });
